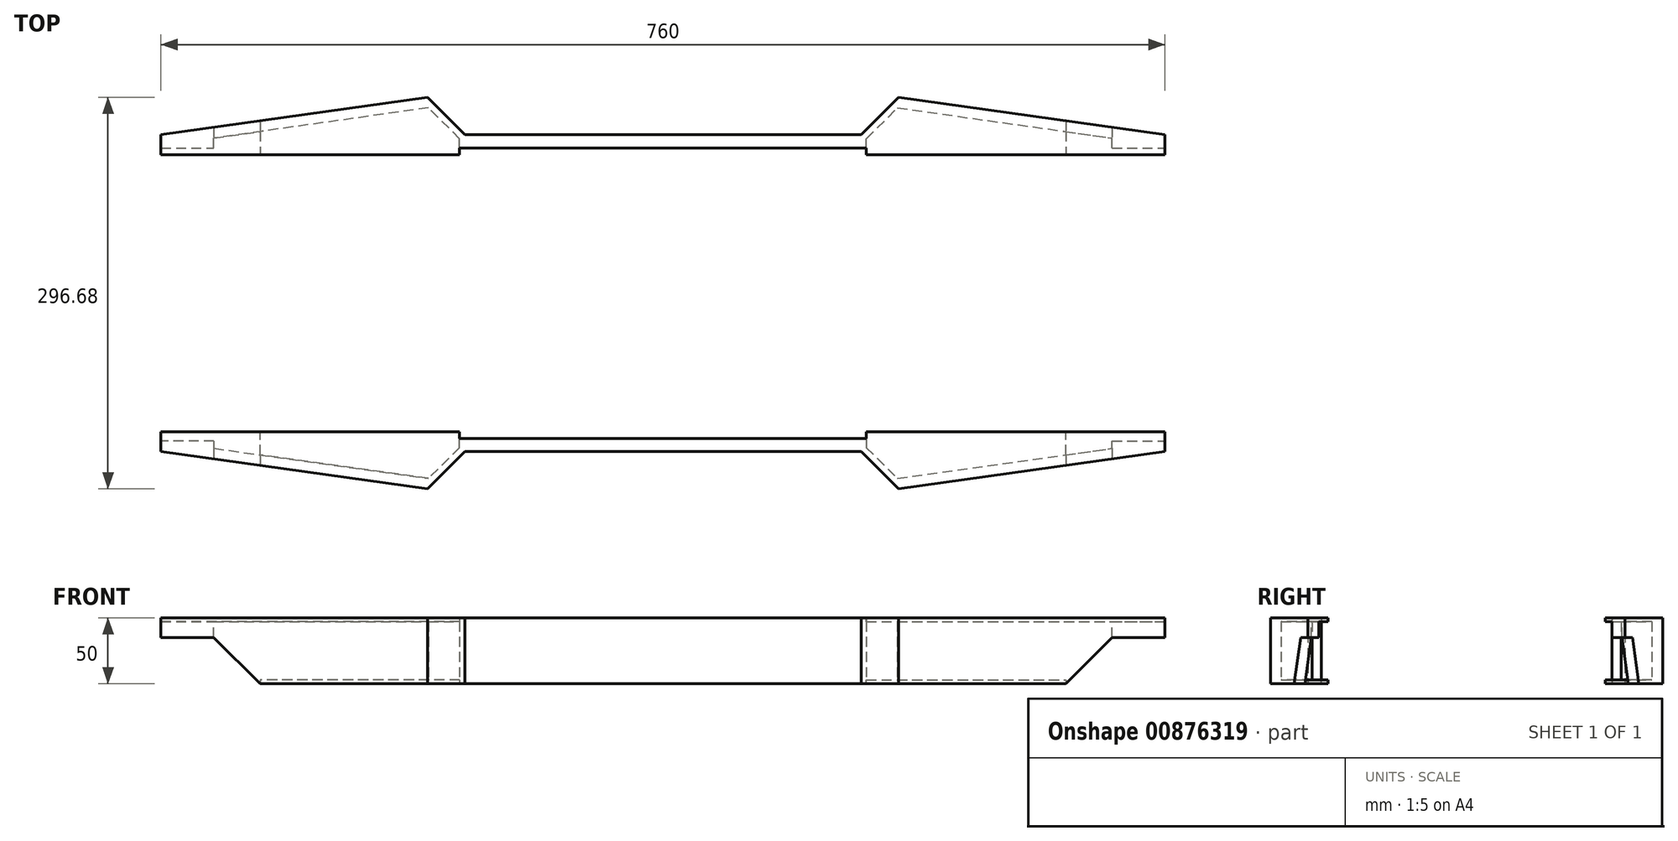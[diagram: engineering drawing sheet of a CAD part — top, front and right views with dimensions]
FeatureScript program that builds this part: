
annotation { "Feature Type Name" : "Feature", "Feature Type Description" : "" }
export const myFeature = defineFeature(function(context is Context, id is Id, definition is map)
    precondition{}
    {
        {
            var Q0;
            Q0=qCreatedBy(makeId("Top.planeOp"),FACE);
            var sketch = newSketch(context, id + "F0", { "sketchPlane" : qUnion([Q0])});
            skLineSegment(sketch, "E0", {"start": v(-380, 120) * mm, "end": v(-380, -120) * mm});
            skLineSegment(sketch, "E1", {"start": v(380, 120) * mm, "end": v(380, -120) * mm});
            skLineSegment(sketch, "E2", {"start": v(150, -120) * mm, "end": v(-150, -120) * mm});
            skLineSegment(sketch, "E3", {"start": v(-150, 120) * mm, "end": v(150, 120) * mm});
            skLineSegment(sketch, "E4", {"start": v(-160, 110) * mm, "end": v(160, 110) * mm, "construction": true});
            skLineSegment(sketch, "E5", {"start": v(160, 110) * mm, "end": v(160, -110) * mm, "construction": true});
            skLineSegment(sketch, "E6", {"start": v(160, -110) * mm, "end": v(-160, -110) * mm, "construction": true});
            skLineSegment(sketch, "E7", {"start": v(-160, -110) * mm, "end": v(-160, 110) * mm, "construction": true});
            skLineSegment(sketch, "E8.0", {"start": v(-150, -110) * mm, "end": v(-150, 110) * mm, "construction": true});
            skLineSegment(sketch, "E9.0", {"start": v(150, 110) * mm, "end": v(150, -110) * mm, "construction": true});
            skLineSegment(sketch, "E10", {"start": v(-150, -110) * mm, "end": v(-150, -120) * mm, "construction": true});
            skLineSegment(sketch, "E11", {"start": v(-150, 110) * mm, "end": v(-150, 120) * mm, "construction": true});
            skLineSegment(sketch, "E12", {"start": v(-150, 120) * mm, "end": v(-178.34, 148.34) * mm});
            skLineSegment(sketch, "E13", {"start": v(-380, 120) * mm, "end": v(-178.34, 148.34) * mm});
            skPoint(sketch, "E14.endSnap0", {"position": v(0, 110) * mm});
            skLineSegment(sketch, "E15.MirrorCS", {"start": v(150, 120) * mm, "end": v(178.34, 148.34) * mm});
            skLineSegment(sketch, "E16.MirrorCS", {"start": v(380, 120) * mm, "end": v(178.34, 148.34) * mm});
            skLineSegment(sketch, "E17.MirrorCS", {"start": v(-150, -120) * mm, "end": v(-178.34, -148.34) * mm, "construction": true});
            skLineSegment(sketch, "E18.MirrorCS", {"start": v(-380, -120) * mm, "end": v(-178.34, -148.34) * mm});
            skLineSegment(sketch, "E19.MirrorCS", {"start": v(150, -120) * mm, "end": v(178.34, -148.34) * mm});
            skLineSegment(sketch, "E20.MirrorCS", {"start": v(-150, -120) * mm, "end": v(-178.34, -148.34) * mm});
            skLineSegment(sketch, "E21.MirrorCS", {"start": v(380, -120) * mm, "end": v(178.34, -148.34) * mm});
            skSolve(sketch);
        }
        {
            var Q0;
            Q0=makeQuery(id+"F0.imprint","IMPRINT",FACE,{"disambiguationData":[TD([[makeQuery(id+"F0.imprint","IMPRINT",EDGE,{"derivedFrom":sQuery(id+"F0.wireOp",EDGE,"E0")}),1.0]])]});
            extrude(context, id + "F1", {"entities" : qUnion([Q0]), "depth" : 50 * mm, "offsetDistance" : 25 * mm});
        }
        {
            var Q0;
            Q0=makeQuery(id+"F1.opExtrude","SWEPT_FACE",FACE,{"disambiguationData":[OSD([sQuery(id+"F0.wireOp",EDGE,"E2")])]});
            var sketch = newSketch(context, id + "F2", { "sketchPlane" : qUnion([Q0])});
            skLineSegment(sketch, "E22", {"start": v(-380, 35) * mm, "end": v(-340, 35) * mm});
            skLineSegment(sketch, "E23", {"start": v(-340, 35) * mm, "end": v(-305, 0) * mm});
            skLineSegment(sketch, "E24", {"start": v(-380, 35) * mm, "end": v(-380, 0) * mm});
            skLineSegment(sketch, "E25", {"start": v(-380, 0) * mm, "end": v(-305, 0) * mm});
            skLineSegment(sketch, "E26.MirrorCS", {"start": v(380, 0) * mm, "end": v(305, 0) * mm});
            skLineSegment(sketch, "E27.MirrorCS", {"start": v(380, 35) * mm, "end": v(380, 0) * mm});
            skLineSegment(sketch, "E28.MirrorCS", {"start": v(380, 35) * mm, "end": v(340, 35) * mm});
            skLineSegment(sketch, "E29.MirrorCS", {"start": v(340, 35) * mm, "end": v(305, 0) * mm});
            skSolve(sketch);
        }
        {
            var Q0;
            Q0=makeQuery(id+"F1.opExtrude","SWEPT_FACE",FACE,{"disambiguationData":[OSD([sQuery(id+"F0.wireOp",EDGE,"E0")])]});
            var sketch = newSketch(context, id + "F3", { "sketchPlane" : qUnion([Q0])});
            skLineSegment(sketch, "E30.0", {"start": v(-110, 45) * mm, "end": v(110, 45) * mm});
            skLineSegment(sketch, "E31.0", {"start": v(-110, 5) * mm, "end": v(110, 5) * mm});
            skLineSegment(sketch, "E32.0", {"start": v(-110, 5) * mm, "end": v(-110, 45) * mm});
            skLineSegment(sketch, "E33.0", {"start": v(110, 45) * mm, "end": v(110, 5) * mm});
            skSolve(sketch);
        }
        {
            var Q0;
            Q0=makeQuery(id+"F3.imprint","IMPRINT",FACE,{"disambiguationData":[TD([[makeQuery(id+"F3.imprint","IMPRINT",EDGE,{"derivedFrom":sQuery(id+"F3.wireOp",EDGE,"E30.0")}),-1.0]])]});
            extrude(context, id + "F4", {"entities" : qUnion([Q0]), "operationType" : NewBodyOperationType.REMOVE, "oppositeDirection" : true, "depth" : 760 * mm, "offsetDistance" : 25 * mm});
        }
        {
            var Q0;
            Q0=makeQuery(id+"F2.imprint","IMPRINT",FACE,{"disambiguationData":[TD([[makeQuery(id+"F2.imprint","IMPRINT",EDGE,{"derivedFrom":sQuery(id+"F2.wireOp",EDGE,"E26.MirrorCS")}),-1.0]])]});
            var Q1;
            Q1=makeQuery(id+"F2.imprint","IMPRINT",FACE,{"disambiguationData":[TD([[makeQuery(id+"F2.imprint","IMPRINT",EDGE,{"derivedFrom":sQuery(id+"F2.wireOp",EDGE,"E22")}),-1.0]])]});
            extrude(context, id + "F5", {"entities" : qUnion([Q0, Q1]), "operationType" : NewBodyOperationType.REMOVE, "oppositeDirection" : true, "depth" : 240 * mm, "offsetDistance" : 25 * mm});
        }
        {
            var Q0;
            Q0=makeQuery(id+"F1.opExtrude","CAP_FACE",FACE,{"disambiguationData":[OSD([sQuery(id+"F0.wireOp",EDGE,"E0"),sQuery(id+"F0.wireOp",EDGE,"E1"),sQuery(id+"F0.wireOp",EDGE,"E2"),sQuery(id+"F0.wireOp",EDGE,"E3")])],"isStart":false});
            var sketch = newSketch(context, id + "F6", { "sketchPlane" : qUnion([Q0])});
            skLineSegment(sketch, "E34", {"start": v(-140, 90) * mm, "end": v(140, 90) * mm});
            skLineSegment(sketch, "E35", {"start": v(140, 90) * mm, "end": v(140, -90) * mm});
            skLineSegment(sketch, "E36", {"start": v(140, -90) * mm, "end": v(-140, -90) * mm});
            skLineSegment(sketch, "E37", {"start": v(-140, -90) * mm, "end": v(-140, 90) * mm});
            skLineSegment(sketch, "E38", {"start": v(160, 110) * mm, "end": v(160, -110) * mm});
            skLineSegment(sketch, "E39", {"start": v(-160, 110) * mm, "end": v(-160, -110) * mm});
            skLineSegment(sketch, "E40", {"start": v(-160, 110) * mm, "end": v(160, 110) * mm});
            skLineSegment(sketch, "E41", {"start": v(160, -110) * mm, "end": v(-160, -110) * mm});
            skSolve(sketch);
        }
        {
            var Q0;
            Q0=qSketchRegion(id+"F6",true);
            extrude(context, id + "F7", {"entities" : qUnion([Q0]), "operationType" : NewBodyOperationType.REMOVE, "oppositeDirection" : true, "depth" : 50 * mm, "offsetDistance" : 25 * mm});
        }
        {
            var Q0;
            Q0=qSketchRegion(id+"F2",true);
            extrude(context, id + "F8", {"entities" : qUnion([Q0]), "operationType" : NewBodyOperationType.REMOVE, "endBound" : BoundingType.SYMMETRIC, "oppositeDirection" : true, "depth" : 871.86 * mm, "offsetDistance" : 25 * mm});
        }
        {
            var Q0;
            {var subQ0=sQuery(id+"F0.wireOp",EDGE,"E18.MirrorCS");var subQ1=sQuery(id+"F0.wireOp",EDGE,"E16.MirrorCS");var subQ2=sQuery(id+"F0.wireOp",EDGE,"E15.MirrorCS");var subQ3=sQuery(id+"F0.wireOp",EDGE,"E13");var subQ4=sQuery(id+"F0.wireOp",EDGE,"E12");var subQ5=sQuery(id+"F0.wireOp",EDGE,"E19.MirrorCS");var subQ6=sQuery(id+"F0.wireOp",EDGE,"E0");var subQ7=sQuery(id+"F0.wireOp",EDGE,"E3");var subQ8=sQuery(id+"F0.wireOp",EDGE,"E1");var subQ9=sQuery(id+"F0.wireOp",EDGE,"E2");var subQ10=sQuery(id+"F0.wireOp",EDGE,"E20.MirrorCS");var subQ11=sQuery(id+"F0.wireOp",EDGE,"E21.MirrorCS");Q0=makeQuery(id+"F7.boolean.opBoolean","SPLIT",FACE,{"disambiguationData":[TD([makeQuery(id+"F1.opExtrude","SWEPT_FACE",FACE,{"disambiguationData":[OSD([subQ6])]})])],"derivedFrom":makeQuery(id+"F1.opExtrude","CAP_FACE",FACE,{"disambiguationData":[OSD([subQ6,subQ8,subQ9,subQ7,subQ4,subQ3,subQ2,subQ1,subQ0,subQ5,subQ10,subQ11])],"isStart":false})});}
            var sketch = newSketch(context, id + "F9", { "sketchPlane" : qUnion([Q0])});
            skLineSegment(sketch, "E42", {"start": v(-165, -110) * mm, "end": v(-305, -110) * mm});
            skLineSegment(sketch, "E43", {"start": v(-305, -110) * mm, "end": v(-305, 110) * mm});
            skLineSegment(sketch, "E44", {"start": v(-305, 110) * mm, "end": v(-165, 110) * mm});
            skLineSegment(sketch, "E45.0", {"start": v(-165, 110) * mm, "end": v(-165, -110) * mm});
            skLineSegment(sketch, "E46", {"start": v(0, 0) * mm, "end": v(0, 58.76) * mm});
            skLineSegment(sketch, "E47.MirrorCS", {"start": v(165, 110) * mm, "end": v(165, -110) * mm});
            skLineSegment(sketch, "E48.MirrorCS", {"start": v(165, -110) * mm, "end": v(305, -110) * mm});
            skLineSegment(sketch, "E49.MirrorCS", {"start": v(305, -110) * mm, "end": v(305, 110) * mm});
            skLineSegment(sketch, "E50.MirrorCS", {"start": v(305, 110) * mm, "end": v(165, 110) * mm});
            skSolve(sketch);
        }
        {
            var Q0;
            Q0=makeQuery(id+"F9.imprint","IMPRINT",FACE,{"disambiguationData":[TD([[makeQuery(id+"F9.imprint","IMPRINT",EDGE,{"derivedFrom":sQuery(id+"F9.wireOp",EDGE,"E42")}),-1.0]])]});
            var Q1;
            Q1=makeQuery(id+"F9.imprint","IMPRINT",FACE,{"disambiguationData":[TD([[makeQuery(id+"F9.imprint","IMPRINT",EDGE,{"derivedFrom":sQuery(id+"F9.wireOp",EDGE,"E47.MirrorCS")}),1.0]])]});
            extrude(context, id + "F10", {"entities" : qUnion([Q0, Q1]), "operationType" : NewBodyOperationType.REMOVE, "oppositeDirection" : true, "depth" : 10 * mm, "offsetDistance" : 25 * mm});
        }
        {
            var Q0;
            Q0=makeQuery(id+"F1.opExtrude","SWEPT_FACE",FACE,{"disambiguationData":[OSD([sQuery(id+"F0.wireOp",EDGE,"E2")])]});
            var sketch = newSketch(context, id + "F11", { "sketchPlane" : qUnion([Q0])});
            skLineSegment(sketch, "E51", {"start": v(-305, 50) * mm, "end": v(-305, 0) * mm});
            skLineSegment(sketch, "E52", {"start": v(-340, 50) * mm, "end": v(-340, 35) * mm});
            skLineSegment(sketch, "E53", {"start": v(-340, 35) * mm, "end": v(-305, 0) * mm});
            skLineSegment(sketch, "E54.0", {"start": v(-332.93, 35) * mm, "end": v(-305, 7.07) * mm});
            skLineSegment(sketch, "E55", {"start": v(-340, 35) * mm, "end": v(-332.93, 35) * mm});
            skLineSegment(sketch, "E56", {"start": v(0, 0) * mm, "end": v(0, 50) * mm});
            skLineSegment(sketch, "E57", {"start": v(-340, 35) * mm, "end": v(-346.55, 35) * mm});
            skLineSegment(sketch, "E58.MirrorCS", {"start": v(332.93, 35) * mm, "end": v(305, 7.07) * mm});
            skLineSegment(sketch, "E59.MirrorCS", {"start": v(340, 35) * mm, "end": v(305, 0) * mm});
            skLineSegment(sketch, "E60.MirrorCS", {"start": v(340, 35) * mm, "end": v(332.93, 35) * mm});
            skLineSegment(sketch, "E61", {"start": v(305, 7.07) * mm, "end": v(305, 0) * mm});
            skSolve(sketch);
        }
        {
            var Q0;
            {var subQ0=sQuery(id+"F11.wireOp",EDGE,"E53");Q0=makeQuery(id+"F11.imprint","IMPRINT",FACE,{"disambiguationData":[TD([[makeQuery(id+"F11.imprint","IMPRINT",EDGE,{"derivedFrom":subQ0}),1.0]])]});}
            var Q1;
            Q1=makeQuery(id+"F11.imprint","IMPRINT",FACE,{"disambiguationData":[TD([[makeQuery(id+"F11.imprint","IMPRINT",EDGE,{"derivedFrom":sQuery(id+"F11.wireOp",EDGE,"E58.MirrorCS")}),1.0]])]});
            extrude(context, id + "F12", {"entities" : qUnion([Q0, Q1]), "oppositeDirection" : true, "depth" : 240 * mm, "offsetDistance" : 25 * mm});
        }
        {
            var Q0;
            Q0=makeQuery(id+"F7.boolean.opBoolean","SPLIT",FACE,{"disambiguationData":[TD([makeQuery(id+"F7.opExtrude","SWEPT_FACE",FACE,{"disambiguationData":[OSD([sQuery(id+"F6.wireOp",EDGE,"E34")])]})])],"derivedFrom":makeQuery(id+"F1.opExtrude","CAP_FACE",FACE,{"disambiguationData":[OSD([sQuery(id+"F0.wireOp",EDGE,"E0"),sQuery(id+"F0.wireOp",EDGE,"E1"),sQuery(id+"F0.wireOp",EDGE,"E2"),sQuery(id+"F0.wireOp",EDGE,"E3"),sQuery(id+"F0.wireOp",EDGE,"E12"),sQuery(id+"F0.wireOp",EDGE,"E13"),sQuery(id+"F0.wireOp",EDGE,"E15.MirrorCS"),sQuery(id+"F0.wireOp",EDGE,"E16.MirrorCS"),sQuery(id+"F0.wireOp",EDGE,"E18.MirrorCS"),sQuery(id+"F0.wireOp",EDGE,"E19.MirrorCS"),sQuery(id+"F0.wireOp",EDGE,"E20.MirrorCS"),sQuery(id+"F0.wireOp",EDGE,"E21.MirrorCS")])],"isStart":false})});
            extrude(context, id + "F13", {"entities" : qUnion([Q0]), "operationType" : NewBodyOperationType.REMOVE, "oppositeDirection" : true, "depth" : 25 * mm, "offsetDistance" : 25 * mm});
        }
        {
            var Q0;
            Q0=makeQuery(id+"F7.boolean.opBoolean","SPLIT",FACE,{"disambiguationData":[TD([makeQuery(id+"F7.opExtrude","SWEPT_FACE",FACE,{"disambiguationData":[OSD([sQuery(id+"F6.wireOp",EDGE,"E34")])]})])],"derivedFrom":makeQuery(id+"F1.opExtrude","CAP_FACE",FACE,{"disambiguationData":[OSD([sQuery(id+"F0.wireOp",EDGE,"E0"),sQuery(id+"F0.wireOp",EDGE,"E1"),sQuery(id+"F0.wireOp",EDGE,"E2"),sQuery(id+"F0.wireOp",EDGE,"E3"),sQuery(id+"F0.wireOp",EDGE,"E12"),sQuery(id+"F0.wireOp",EDGE,"E13"),sQuery(id+"F0.wireOp",EDGE,"E15.MirrorCS"),sQuery(id+"F0.wireOp",EDGE,"E16.MirrorCS"),sQuery(id+"F0.wireOp",EDGE,"E18.MirrorCS"),sQuery(id+"F0.wireOp",EDGE,"E19.MirrorCS"),sQuery(id+"F0.wireOp",EDGE,"E20.MirrorCS"),sQuery(id+"F0.wireOp",EDGE,"E21.MirrorCS")])],"isStart":true})});
            extrude(context, id + "F14", {"entities" : qUnion([Q0]), "operationType" : NewBodyOperationType.REMOVE, "oppositeDirection" : true, "depth" : 25 * mm, "offsetDistance" : 25 * mm});
        }
        {
            var Q0;
            Q0=makeQuery(id+"F7.boolean.opBoolean","COPY",FACE,{"disambiguationData":[TD([makeQuery(id+"F4.boolean.opBoolean","COPY",FACE,{"derivedFrom":makeQuery(id+"F4.opExtrude","SWEPT_FACE",FACE,{"disambiguationData":[OSD([sQuery(id+"F3.wireOp",EDGE,"E30.0")])]})})])],"derivedFrom":makeQuery(id+"F7.opExtrude","SWEPT_FACE",FACE,{"disambiguationData":[OSD([sQuery(id+"F6.wireOp",EDGE,"E38")])]})});
            var sketch = newSketch(context, id + "F15", { "sketchPlane" : qUnion([Q0])});
            skLineSegment(sketch, "E62", {"start": v(-110, 45) * mm, "end": v(-110, 5) * mm});
            skLineSegment(sketch, "E63", {"start": v(-110, 45) * mm, "end": v(110, 45) * mm});
            skLineSegment(sketch, "E64", {"start": v(110, 45) * mm, "end": v(110, 5) * mm});
            skLineSegment(sketch, "E65", {"start": v(-110, 5) * mm, "end": v(110, 5) * mm});
            skSolve(sketch);
        }
        {
            var Q0;
            Q0=makeQuery(id+"F7.boolean.opBoolean","COPY",FACE,{"disambiguationData":[TD([makeQuery(id+"F4.boolean.opBoolean","COPY",FACE,{"derivedFrom":makeQuery(id+"F4.opExtrude","SWEPT_FACE",FACE,{"disambiguationData":[OSD([sQuery(id+"F3.wireOp",EDGE,"E31.0")])]})})])],"derivedFrom":makeQuery(id+"F7.opExtrude","SWEPT_FACE",FACE,{"disambiguationData":[OSD([sQuery(id+"F6.wireOp",EDGE,"E39")])]})});
            var sketch = newSketch(context, id + "F16", { "sketchPlane" : qUnion([Q0])});
            skLineSegment(sketch, "E66", {"start": v(-110, 5) * mm, "end": v(-110, 45) * mm});
            skLineSegment(sketch, "E67", {"start": v(-110, 5) * mm, "end": v(110, 5) * mm});
            skLineSegment(sketch, "E68", {"start": v(110, 5) * mm, "end": v(110, 45) * mm});
            skLineSegment(sketch, "E69", {"start": v(-110, 45) * mm, "end": v(110, 45) * mm});
            skSolve(sketch);
        }
        {
            var Q0;
            Q0=qSketchRegion(id+"F16",true);
            extrude(context, id + "F17", {"entities" : qUnion([Q0]), "operationType" : NewBodyOperationType.ADD, "oppositeDirection" : true, "depth" : 5 * mm, "offsetDistance" : 25 * mm});
        }
        {
            var Q0;
            Q0=makeQuery(id+"F15.imprint","IMPRINT",FACE,{"disambiguationData":[TD([[makeQuery(id+"F15.imprint","IMPRINT",EDGE,{"derivedFrom":sQuery(id+"F15.wireOp",EDGE,"E62")}),1.0]])]});
            extrude(context, id + "F18", {"entities" : qUnion([Q0]), "operationType" : NewBodyOperationType.ADD, "oppositeDirection" : true, "depth" : 5 * mm, "offsetDistance" : 25 * mm});
        }
        {
            var Q0;
            Q0=makeQuery(id+"F7.boolean.opBoolean","SPLIT",BODY,{"disambiguationData":[OD(0.0)],"derivedFrom":makeQuery(id+"F1.opExtrude","SWEPT_BODY",BODY,{"disambiguationData":[OSD([sQuery(id+"F0.wireOp",EDGE,"E0"),sQuery(id+"F0.wireOp",EDGE,"E1"),sQuery(id+"F0.wireOp",EDGE,"E2"),sQuery(id+"F0.wireOp",EDGE,"E3"),sQuery(id+"F0.wireOp",EDGE,"E12"),sQuery(id+"F0.wireOp",EDGE,"E13"),sQuery(id+"F0.wireOp",EDGE,"E15.MirrorCS"),sQuery(id+"F0.wireOp",EDGE,"E16.MirrorCS"),sQuery(id+"F0.wireOp",EDGE,"E18.MirrorCS"),sQuery(id+"F0.wireOp",EDGE,"E19.MirrorCS"),sQuery(id+"F0.wireOp",EDGE,"E20.MirrorCS"),sQuery(id+"F0.wireOp",EDGE,"E21.MirrorCS")])]})});
            var Q1;
            Q1=makeQuery(id+"F12.opExtrude","SWEPT_BODY",BODY,{"disambiguationData":[OSD([sQuery(id+"F11.wireOp",EDGE,"E51"),sQuery(id+"F11.wireOp",EDGE,"E53"),sQuery(id+"F11.wireOp",EDGE,"E54.0"),sQuery(id+"F11.wireOp",EDGE,"E55")])]});
            var Q2;
            Q2=makeQuery(id+"F12.opExtrude","SWEPT_BODY",BODY,{"disambiguationData":[OSD([sQuery(id+"F11.wireOp",EDGE,"E58.MirrorCS"),sQuery(id+"F11.wireOp",EDGE,"E59.MirrorCS"),sQuery(id+"F11.wireOp",EDGE,"E60.MirrorCS"),sQuery(id+"F11.wireOp",EDGE,"E61")])]});
            booleanBodies(context, id + "F19", {"operationType" : BooleanOperationType.UNION, "tools" : qUnion([Q0, Q1, Q2])});
        }
        {
            var Q0;
            Q0=makeQuery(id+"F10.boolean.opBoolean","COPY",FACE,{"derivedFrom":makeQuery(id+"F10.opExtrude","SWEPT_FACE",FACE,{"disambiguationData":[OSD([sQuery(id+"F9.wireOp",EDGE,"E43")])]})});
            extrude(context, id + "F20", {"entities" : qUnion([Q0]), "operationType" : NewBodyOperationType.REMOVE, "oppositeDirection" : true, "depth" : 121.6 * mm, "offsetDistance" : 25 * mm});
        }
        {
            var Q0;
            Q0=makeQuery(id+"F10.boolean.opBoolean","COPY",FACE,{"derivedFrom":makeQuery(id+"F10.opExtrude","SWEPT_FACE",FACE,{"disambiguationData":[OSD([sQuery(id+"F9.wireOp",EDGE,"E49.MirrorCS")])]})});
            extrude(context, id + "F21", {"entities" : qUnion([Q0]), "operationType" : NewBodyOperationType.REMOVE, "endBound" : BoundingType.SYMMETRIC, "depth" : 2865.48 * mm, "offsetDistance" : 25 * mm});
        }
        {
            var Q0;
            Q0=makeQuery(id+"F17.boolean.opBoolean","MERGE",FACE,{"derivedFrom":[makeQuery(id+"F10.boolean.opBoolean","COPY",FACE,{"derivedFrom":makeQuery(id+"F10.opExtrude","SWEPT_FACE",FACE,{"disambiguationData":[OSD([sQuery(id+"F9.wireOp",EDGE,"E45.0")])]})}),makeQuery(id+"F17.opExtrude","CAP_FACE",FACE,{"disambiguationData":[OSD([sQuery(id+"F16.wireOp",EDGE,"E66"),sQuery(id+"F16.wireOp",EDGE,"E67"),sQuery(id+"F16.wireOp",EDGE,"E68"),sQuery(id+"F16.wireOp",EDGE,"E69")])],"isStart":false})]});
            extrude(context, id + "F22", {"entities" : qUnion([Q0]), "operationType" : NewBodyOperationType.REMOVE, "endBound" : BoundingType.SYMMETRIC, "oppositeDirection" : true, "depth" : 1589.2 * mm, "offsetDistance" : 25 * mm});
        }
        {
            var Q0;
            {var subQ16=makeQuery(id+"F7.opExtrude","SWEPT_FACE",FACE,{"disambiguationData":[OSD([sQuery(id+"F6.wireOp",EDGE,"E39")])]});Q0=makeQuery(id+"F17.boolean.opBoolean","MERGE",FACE,{"derivedFrom":[makeQuery(id+"F7.boolean.opBoolean","COPY",FACE,{"disambiguationData":[TD([makeQuery(id+"F4.boolean.opBoolean","COPY",FACE,{"derivedFrom":makeQuery(id+"F4.opExtrude","SWEPT_FACE",FACE,{"disambiguationData":[OSD([sQuery(id+"F3.wireOp",EDGE,"E30.0")])]})})])],"derivedFrom":subQ16}),makeQuery(id+"F7.boolean.opBoolean","COPY",FACE,{"disambiguationData":[TD([makeQuery(id+"F4.boolean.opBoolean","COPY",FACE,{"derivedFrom":makeQuery(id+"F4.opExtrude","SWEPT_FACE",FACE,{"disambiguationData":[OSD([sQuery(id+"F3.wireOp",EDGE,"E31.0")])]})})])],"derivedFrom":subQ16}),makeQuery(id+"F17.opExtrude","CAP_FACE",FACE,{"disambiguationData":[OSD([sQuery(id+"F16.wireOp",EDGE,"E66"),sQuery(id+"F16.wireOp",EDGE,"E67"),sQuery(id+"F16.wireOp",EDGE,"E68"),sQuery(id+"F16.wireOp",EDGE,"E69")])],"isStart":true})]});}
            extrude(context, id + "F23", {"entities" : qUnion([Q0]), "operationType" : NewBodyOperationType.REMOVE, "endBound" : BoundingType.SYMMETRIC, "depth" : 1696.6 * mm, "offsetDistance" : 25 * mm});
        }
        {
            var Q0;
            {var subQ1=sQuery(id+"F0.wireOp",EDGE,"E19.MirrorCS");var subQ3=sQuery(id+"F0.wireOp",EDGE,"E21.MirrorCS");var subQ7=sQuery(id+"F0.wireOp",EDGE,"E2");var subQ8=makeQuery(id+"F1.opExtrude","SWEPT_FACE",FACE,{"disambiguationData":[OSD([subQ7])]});var subQ9=sQuery(id+"F0.wireOp",EDGE,"E18.MirrorCS");var subQ13=sQuery(id+"F0.wireOp",EDGE,"E20.MirrorCS");var subQ17=sQuery(id+"F0.wireOp",EDGE,"E16.MirrorCS");var subQ18=sQuery(id+"F0.wireOp",EDGE,"E15.MirrorCS");var subQ22=sQuery(id+"F0.wireOp",EDGE,"E3");var subQ23=sQuery(id+"F0.wireOp",EDGE,"E12");var subQ27=sQuery(id+"F0.wireOp",EDGE,"E13");Q0=makeQuery(id+"F23.boolean.opBoolean","SPLIT",FACE,{"disambiguationData":[TD([subQ8])],"derivedFrom":makeQuery(id+"F7.boolean.opBoolean","SPLIT",FACE,{"disambiguationData":[TD([subQ8])],"derivedFrom":makeQuery(id+"F1.opExtrude","CAP_FACE",FACE,{"disambiguationData":[OSD([sQuery(id+"F0.wireOp",EDGE,"E0"),sQuery(id+"F0.wireOp",EDGE,"E1"),subQ7,subQ22,subQ23,subQ27,subQ18,subQ17,subQ9,subQ1,subQ13,subQ3])],"isStart":true})})});}
            var sketch = newSketch(context, id + "F24", { "sketchPlane" : qUnion([Q0])});
            skLineSegment(sketch, "E70", {"start": v(-301, 110) * mm, "end": v(-154, 110) * mm});
            skLineSegment(sketch, "E71.0", {"start": v(-177.46, 140.39) * mm, "end": v(-301, 123.02) * mm});
            skLineSegment(sketch, "E72.0", {"start": v(-301, 123.02) * mm, "end": v(-301, 110) * mm});
            skLineSegment(sketch, "E73.0", {"start": v(-154, 116.93) * mm, "end": v(-177.46, 140.39) * mm});
            skLineSegment(sketch, "E74.0", {"start": v(-154, 110) * mm, "end": v(-154, 116.93) * mm});
            skLineSegment(sketch, "E75.MirrorCS", {"start": v(-301, -110) * mm, "end": v(-154, -110) * mm});
            skLineSegment(sketch, "E76.MirrorCS", {"start": v(-177.46, -140.39) * mm, "end": v(-301, -123.02) * mm});
            skLineSegment(sketch, "E77.MirrorCS", {"start": v(-301, -123.02) * mm, "end": v(-301, -110) * mm});
            skLineSegment(sketch, "E78.MirrorCS", {"start": v(-154, -116.93) * mm, "end": v(-177.46, -140.39) * mm});
            skLineSegment(sketch, "E79.MirrorCS", {"start": v(-154, -110) * mm, "end": v(-154, -116.93) * mm});
            skLineSegment(sketch, "E80.MirrorCS", {"start": v(154, 116.93) * mm, "end": v(177.46, 140.39) * mm});
            skLineSegment(sketch, "E81.MirrorCS", {"start": v(301, 110) * mm, "end": v(154, 110) * mm});
            skLineSegment(sketch, "E82.MirrorCS", {"start": v(301, -110) * mm, "end": v(154, -110) * mm});
            skLineSegment(sketch, "E83.MirrorCS", {"start": v(154, 110) * mm, "end": v(154, 116.93) * mm});
            skLineSegment(sketch, "E84.MirrorCS", {"start": v(177.46, 140.39) * mm, "end": v(301, 123.02) * mm});
            skLineSegment(sketch, "E85.MirrorCS", {"start": v(301, 123.02) * mm, "end": v(301, 110) * mm});
            skLineSegment(sketch, "E86.MirrorCS", {"start": v(154, -110) * mm, "end": v(154, -116.93) * mm});
            skLineSegment(sketch, "E87.MirrorCS", {"start": v(154, -116.93) * mm, "end": v(177.46, -140.39) * mm});
            skLineSegment(sketch, "E88.MirrorCS", {"start": v(301, -123.02) * mm, "end": v(301, -110) * mm});
            skLineSegment(sketch, "E89.MirrorCS", {"start": v(177.46, -140.39) * mm, "end": v(301, -123.02) * mm});
            skSolve(sketch);
        }
        {
            var Q0;
            Q0=makeQuery(id+"F24.imprint","IMPRINT",FACE,{"disambiguationData":[TD([[makeQuery(id+"F24.imprint","IMPRINT",EDGE,{"derivedFrom":sQuery(id+"F24.wireOp",EDGE,"E75.MirrorCS")}),-1.0]])]});
            var Q1;
            Q1=makeQuery(id+"F24.imprint","IMPRINT",FACE,{"disambiguationData":[TD([[makeQuery(id+"F24.imprint","IMPRINT",EDGE,{"derivedFrom":sQuery(id+"F24.wireOp",EDGE,"E86.MirrorCS")}),1.0]])]});
            extrude(context, id + "F25", {"entities" : qUnion([Q0, Q1]), "operationType" : NewBodyOperationType.REMOVE, "oppositeDirection" : true, "depth" : 50 * mm, "offsetDistance" : 25 * mm});
        }
        {
            var Q0;
            Q0=makeQuery(id+"F24.imprint","IMPRINT",FACE,{"disambiguationData":[TD([[makeQuery(id+"F24.imprint","IMPRINT",EDGE,{"derivedFrom":sQuery(id+"F24.wireOp",EDGE,"E70")}),-1.0]])]});
            var Q1;
            Q1=makeQuery(id+"F24.imprint","IMPRINT",FACE,{"disambiguationData":[TD([[makeQuery(id+"F24.imprint","IMPRINT",EDGE,{"derivedFrom":sQuery(id+"F24.wireOp",EDGE,"E80.MirrorCS")}),-1.0]])]});
            extrude(context, id + "F26", {"entities" : qUnion([Q0, Q1]), "operationType" : NewBodyOperationType.REMOVE, "oppositeDirection" : true, "depth" : 50 * mm, "offsetDistance" : 25 * mm});
        }
        {
            var Q0;
            {var subQ0=sQuery(id+"F0.wireOp",EDGE,"E2");var subQ1=makeQuery(id+"F1.opExtrude","SWEPT_FACE",FACE,{"disambiguationData":[OSD([subQ0])]});var subQ2=sQuery(id+"F0.wireOp",EDGE,"E1");var subQ4=sQuery(id+"F0.wireOp",EDGE,"E18.MirrorCS");var subQ6=sQuery(id+"F0.wireOp",EDGE,"E0");var subQ7=makeQuery(id+"F1.opExtrude","SWEPT_FACE",FACE,{"disambiguationData":[OSD([subQ6])]});var subQ8=sQuery(id+"F0.wireOp",EDGE,"E19.MirrorCS");var subQ10=sQuery(id+"F0.wireOp",EDGE,"E20.MirrorCS");var subQ12=sQuery(id+"F0.wireOp",EDGE,"E21.MirrorCS");var subQ15=sQuery(id+"F0.wireOp",EDGE,"E16.MirrorCS");var subQ16=sQuery(id+"F0.wireOp",EDGE,"E15.MirrorCS");var subQ17=sQuery(id+"F0.wireOp",EDGE,"E13");var subQ18=sQuery(id+"F0.wireOp",EDGE,"E12");var subQ19=sQuery(id+"F0.wireOp",EDGE,"E3");Q0=makeQuery(id+"F21.boolean.opBoolean","SPLIT",FACE,{"disambiguationData":[TD([subQ1])],"derivedFrom":makeQuery(id+"F7.boolean.opBoolean","SPLIT",FACE,{"disambiguationData":[TD([subQ7])],"derivedFrom":makeQuery(id+"F1.opExtrude","CAP_FACE",FACE,{"disambiguationData":[OSD([subQ6,subQ2,subQ0,subQ19,subQ18,subQ17,subQ16,subQ15,subQ4,subQ8,subQ10,subQ12])],"isStart":false})})});}
            var sketch = newSketch(context, id + "F27", { "sketchPlane" : qUnion([Q0])});
            skLineSegment(sketch, "E90.0", {"start": v(301, -123.02) * mm, "end": v(340, -117.54) * mm});
            skLineSegment(sketch, "E91", {"start": v(340, -110) * mm, "end": v(340, -117.54) * mm});
            skLineSegment(sketch, "E92", {"start": v(301, -110) * mm, "end": v(340, -110) * mm});
            skLineSegment(sketch, "E93", {"start": v(301, -110) * mm, "end": v(301, -123.02) * mm});
            skLineSegment(sketch, "E94.MirrorCS", {"start": v(-301, -110) * mm, "end": v(-301, -123.02) * mm});
            skLineSegment(sketch, "E95.MirrorCS", {"start": v(-301, -110) * mm, "end": v(-340, -110) * mm});
            skLineSegment(sketch, "E96.MirrorCS", {"start": v(-340, -110) * mm, "end": v(-340, -117.54) * mm});
            skLineSegment(sketch, "E97.MirrorCS", {"start": v(-301, -123.02) * mm, "end": v(-340, -117.54) * mm});
            skLineSegment(sketch, "E98.MirrorCS", {"start": v(340, 110) * mm, "end": v(340, 117.54) * mm});
            skLineSegment(sketch, "E99.MirrorCS", {"start": v(301, 110) * mm, "end": v(340, 110) * mm});
            skLineSegment(sketch, "E100.MirrorCS", {"start": v(301, 123.02) * mm, "end": v(340, 117.54) * mm});
            skLineSegment(sketch, "E101.MirrorCS", {"start": v(301, 110) * mm, "end": v(301, 123.02) * mm});
            skLineSegment(sketch, "E102.MirrorCS", {"start": v(-301, 110) * mm, "end": v(-301, 123.02) * mm});
            skLineSegment(sketch, "E103.MirrorCS", {"start": v(-301, 110) * mm, "end": v(-340, 110) * mm});
            skLineSegment(sketch, "E104.MirrorCS", {"start": v(-301, 123.02) * mm, "end": v(-340, 117.54) * mm});
            skLineSegment(sketch, "E105.MirrorCS", {"start": v(-340, 110) * mm, "end": v(-340, 117.54) * mm});
            skSolve(sketch);
        }
        {
            var Q0;
            Q0=qSketchRegion(id+"F27",true);
            extrude(context, id + "F28", {"entities" : qUnion([Q0]), "operationType" : NewBodyOperationType.REMOVE, "oppositeDirection" : true, "depth" : 50 * mm, "offsetDistance" : 25 * mm});
        }
        {
            var Q0;
            Q0=makeQuery(id+"F26.boolean.opBoolean","COPY",FACE,{"derivedFrom":makeQuery(id+"F26.opExtrude","SWEPT_FACE",FACE,{"disambiguationData":[OSD([sQuery(id+"F24.wireOp",EDGE,"E83.MirrorCS")])]})});
            var sketch = newSketch(context, id + "F29", { "sketchPlane" : qUnion([Q0])});
            skLineSegment(sketch, "E106", {"start": v(-110, 47) * mm, "end": v(-110, 3) * mm});
            skLineSegment(sketch, "E107.0", {"start": v(-112, 47) * mm, "end": v(-112, 3) * mm});
            skLineSegment(sketch, "E108.MirrorCS", {"start": v(110, 47) * mm, "end": v(110, 3) * mm});
            skLineSegment(sketch, "E109.MirrorCS", {"start": v(112, 47) * mm, "end": v(112, 3) * mm});
            skLineSegment(sketch, "E110", {"start": v(-110, 3) * mm, "end": v(-112, 3) * mm});
            skLineSegment(sketch, "E111", {"start": v(-110, 47) * mm, "end": v(-112, 47) * mm});
            skLineSegment(sketch, "E112.MirrorCS", {"start": v(110, 3) * mm, "end": v(112, 3) * mm});
            skLineSegment(sketch, "E113.MirrorCS", {"start": v(110, 47) * mm, "end": v(112, 47) * mm});
            skSolve(sketch);
        }
        {
            var Q0;
            Q0=makeQuery(id+"F29.imprint","IMPRINT",FACE,{"disambiguationData":[TD([[makeQuery(id+"F29.imprint","IMPRINT",EDGE,{"derivedFrom":sQuery(id+"F29.wireOp",EDGE,"E106")}),-1.0]])]});
            var Q1;
            Q1=makeQuery(id+"F29.imprint","IMPRINT",FACE,{"disambiguationData":[TD([[makeQuery(id+"F29.imprint","IMPRINT",EDGE,{"derivedFrom":sQuery(id+"F29.wireOp",EDGE,"ca43fbb2-e32b-444a-a71d-7a7fd8a9ca550.MirrorCS")}),1.0]])]});
            extrude(context, id + "F30", {"entities" : qUnion([Q0, Q1]), "operationType" : NewBodyOperationType.REMOVE, "endBound" : BoundingType.SYMMETRIC, "oppositeDirection" : true, "depth" : 1554.04 * mm, "offsetDistance" : 25 * mm});
        }
        {
            var Q0;
            Q0=makeQuery(id+"F29.imprint","IMPRINT",FACE,{"disambiguationData":[TD([[makeQuery(id+"F29.imprint","IMPRINT",EDGE,{"derivedFrom":sQuery(id+"F29.wireOp",EDGE,"E106")}),-1.0]])]});
            var Q1;
            Q1=makeQuery(id+"F29.imprint","IMPRINT",FACE,{"disambiguationData":[TD([[makeQuery(id+"F29.imprint","IMPRINT",EDGE,{"derivedFrom":sQuery(id+"F29.wireOp",EDGE,"ca43fbb2-e32b-444a-a71d-7a7fd8a9ca550.MirrorCS")}),1.0]])]});
            extrude(context, id + "F31", {"entities" : qUnion([Q0, Q1]), "operationType" : NewBodyOperationType.ADD, "oppositeDirection" : true, "depth" : 308 * mm, "offsetDistance" : 25 * mm});
        }
        {
            var Q0;
            {var subQ0=sQuery(id+"F0.wireOp",EDGE,"E12");var subQ2=sQuery(id+"F0.wireOp",EDGE,"E1");var subQ4=sQuery(id+"F0.wireOp",EDGE,"E3");var subQ5=makeQuery(id+"F1.opExtrude","SWEPT_FACE",FACE,{"disambiguationData":[OSD([subQ4])]});var subQ6=sQuery(id+"F0.wireOp",EDGE,"E0");var subQ7=makeQuery(id+"F1.opExtrude","SWEPT_FACE",FACE,{"disambiguationData":[OSD([subQ6])]});var subQ8=sQuery(id+"F0.wireOp",EDGE,"E13");var subQ10=sQuery(id+"F0.wireOp",EDGE,"E15.MirrorCS");var subQ12=sQuery(id+"F0.wireOp",EDGE,"E16.MirrorCS");var subQ15=sQuery(id+"F0.wireOp",EDGE,"E18.MirrorCS");var subQ16=sQuery(id+"F0.wireOp",EDGE,"E19.MirrorCS");var subQ17=sQuery(id+"F0.wireOp",EDGE,"E2");var subQ18=sQuery(id+"F0.wireOp",EDGE,"E20.MirrorCS");var subQ19=sQuery(id+"F0.wireOp",EDGE,"E21.MirrorCS");Q0=makeQuery(id+"F21.boolean.opBoolean","SPLIT",FACE,{"disambiguationData":[TD([subQ5])],"derivedFrom":makeQuery(id+"F7.boolean.opBoolean","SPLIT",FACE,{"disambiguationData":[TD([subQ7])],"derivedFrom":makeQuery(id+"F1.opExtrude","CAP_FACE",FACE,{"disambiguationData":[OSD([subQ6,subQ2,subQ17,subQ4,subQ0,subQ8,subQ10,subQ12,subQ15,subQ16,subQ18,subQ19])],"isStart":false})})});}
            var sketch = newSketch(context, id + "F32", { "sketchPlane" : qUnion([Q0])});
            skLineSegment(sketch, "E114", {"start": v(380, 110) * mm, "end": v(340, 110) * mm});
            skLineSegment(sketch, "E115", {"start": v(250.64, 241.62) * mm, "end": v(250.64, 241.62) * mm});
            skLineSegment(sketch, "E116.trimOffspring", {"start": v(-340, 110) * mm, "end": v(-380, 110) * mm});
            skLineSegment(sketch, "E117", {"start": v(-340, 105) * mm, "end": v(-380, 105) * mm});
            skLineSegment(sketch, "E118", {"start": v(340, 105) * mm, "end": v(380, 105) * mm});
            skLineSegment(sketch, "E119", {"start": v(380, 110) * mm, "end": v(380, 105) * mm});
            skLineSegment(sketch, "E120", {"start": v(-380, 105) * mm, "end": v(-380, 110) * mm});
            skLineSegment(sketch, "E121.MirrorCS", {"start": v(-154, -110) * mm, "end": v(-154, -105) * mm});
            skLineSegment(sketch, "E122.MirrorCS", {"start": v(-380, -105) * mm, "end": v(-380, -110) * mm});
            skLineSegment(sketch, "E123.MirrorCS", {"start": v(-340, -105) * mm, "end": v(-380, -105) * mm});
            skLineSegment(sketch, "E124.MirrorCS", {"start": v(-340, -110) * mm, "end": v(-380, -110) * mm});
            skLineSegment(sketch, "E125.MirrorCS", {"start": v(-340, -110) * mm, "end": v(-340, -105) * mm});
            skLineSegment(sketch, "E126.MirrorCS", {"start": v(154, -105) * mm, "end": v(154, -110) * mm});
            skLineSegment(sketch, "E127.MirrorCS", {"start": v(340, -105) * mm, "end": v(340, -110) * mm});
            skLineSegment(sketch, "E128.MirrorCS", {"start": v(380, -110) * mm, "end": v(380, -105) * mm});
            skLineSegment(sketch, "E129.MirrorCS", {"start": v(340, -105) * mm, "end": v(380, -105) * mm});
            skLineSegment(sketch, "E130.MirrorCS", {"start": v(380, -110) * mm, "end": v(340, -110) * mm});
            skLineSegment(sketch, "E131", {"start": v(-340, 110) * mm, "end": v(-340, 117.54) * mm});
            skLineSegment(sketch, "E132", {"start": v(-340, 117.54) * mm, "end": v(-177.46, 140.39) * mm});
            skLineSegment(sketch, "E133", {"start": v(-177.46, 140.39) * mm, "end": v(-154, 116.93) * mm});
            skLineSegment(sketch, "E134", {"start": v(-154, 116.93) * mm, "end": v(-154, 110) * mm});
            skLineSegment(sketch, "E135", {"start": v(-154, 105) * mm, "end": v(-340, 105) * mm});
            skLineSegment(sketch, "E136", {"start": v(154, 110) * mm, "end": v(154, 116.93) * mm});
            skLineSegment(sketch, "E137", {"start": v(154, 116.93) * mm, "end": v(177.46, 140.39) * mm});
            skLineSegment(sketch, "E138", {"start": v(177.46, 140.39) * mm, "end": v(340, 117.54) * mm});
            skLineSegment(sketch, "E139", {"start": v(340, 117.54) * mm, "end": v(340, 110) * mm});
            skLineSegment(sketch, "E140", {"start": v(340, 105) * mm, "end": v(154, 105) * mm});
            skLineSegment(sketch, "E141.MirrorCS", {"start": v(-154, -105) * mm, "end": v(-340, -105) * mm});
            skLineSegment(sketch, "E142.MirrorCS", {"start": v(-340, -117.54) * mm, "end": v(-177.46, -140.39) * mm});
            skLineSegment(sketch, "E143.MirrorCS", {"start": v(-340, -110) * mm, "end": v(-340, -117.54) * mm});
            skLineSegment(sketch, "E144.MirrorCS", {"start": v(-177.46, -140.39) * mm, "end": v(-154, -116.93) * mm});
            skLineSegment(sketch, "E145.MirrorCS", {"start": v(-154, -116.93) * mm, "end": v(-154, -110) * mm});
            skLineSegment(sketch, "E146.MirrorCS", {"start": v(154, -116.93) * mm, "end": v(177.46, -140.39) * mm});
            skLineSegment(sketch, "E147.MirrorCS", {"start": v(177.46, -140.39) * mm, "end": v(340, -117.54) * mm});
            skLineSegment(sketch, "E148.MirrorCS", {"start": v(154, -110) * mm, "end": v(154, -116.93) * mm});
            skLineSegment(sketch, "E149.MirrorCS", {"start": v(340, -117.54) * mm, "end": v(340, -110) * mm});
            skLineSegment(sketch, "E150.MirrorCS", {"start": v(340, -105) * mm, "end": v(154, -105) * mm});
            skLineSegment(sketch, "E151", {"start": v(-154, 110) * mm, "end": v(-154, 105) * mm});
            skLineSegment(sketch, "E152.MirrorCS", {"start": v(154, -110) * mm, "end": v(154, -105) * mm});
            skLineSegment(sketch, "E153.MirrorCS", {"start": v(154, 110) * mm, "end": v(154, 105) * mm});
            skSolve(sketch);
        }
        {
            var Q0;
            Q0 = qSketchRegion(id + "F32", true);
            extrude(context, id + "F33", {"entities" : qUnion([Q0]), "operationType" : NewBodyOperationType.ADD, "oppositeDirection" : true, "depth" : 3 * mm, "offsetDistance" : 25 * mm});
        }
        {
            var Q0;
            {var subQ0=sQuery(id+"F0.wireOp",EDGE,"E16.MirrorCS");var subQ4=sQuery(id+"F0.wireOp",EDGE,"E3");var subQ5=makeQuery(id+"F1.opExtrude","SWEPT_FACE",FACE,{"disambiguationData":[OSD([subQ4])]});var subQ8=sQuery(id+"F0.wireOp",EDGE,"E15.MirrorCS");var subQ11=sQuery(id+"F0.wireOp",EDGE,"E12");var subQ13=sQuery(id+"F0.wireOp",EDGE,"E13");var subQ17=sQuery(id+"F0.wireOp",EDGE,"E21.MirrorCS");var subQ18=sQuery(id+"F0.wireOp",EDGE,"E20.MirrorCS");var subQ19=sQuery(id+"F0.wireOp",EDGE,"E19.MirrorCS");var subQ20=sQuery(id+"F0.wireOp",EDGE,"E18.MirrorCS");var subQ21=sQuery(id+"F0.wireOp",EDGE,"E2");Q0=makeQuery(id+"F23.boolean.opBoolean","SPLIT",FACE,{"disambiguationData":[TD([subQ5])],"derivedFrom":makeQuery(id+"F7.boolean.opBoolean","SPLIT",FACE,{"disambiguationData":[TD([makeQuery(id+"F1.opExtrude","SWEPT_FACE",FACE,{"disambiguationData":[OSD([subQ21])]})])],"derivedFrom":makeQuery(id+"F1.opExtrude","CAP_FACE",FACE,{"disambiguationData":[OSD([sQuery(id+"F0.wireOp",EDGE,"E0"),sQuery(id+"F0.wireOp",EDGE,"E1"),subQ21,subQ4,subQ11,subQ13,subQ8,subQ0,subQ20,subQ19,subQ18,subQ17])],"isStart":true})})});}
            var sketch = newSketch(context, id + "F34", { "sketchPlane" : qUnion([Q0])});
            skLineSegment(sketch, "E154", {"start": v(-154, -110) * mm, "end": v(-154, -116.93) * mm});
            skLineSegment(sketch, "E155", {"start": v(-154, -116.93) * mm, "end": v(-177.46, -140.39) * mm});
            skLineSegment(sketch, "E156", {"start": v(-177.46, -140.39) * mm, "end": v(-305, -122.46) * mm});
            skLineSegment(sketch, "E157", {"start": v(-305, -122.46) * mm, "end": v(-305, -110) * mm});
            skLineSegment(sketch, "E158.0", {"start": v(-154, -105) * mm, "end": v(-305, -105) * mm});
            skLineSegment(sketch, "E159", {"start": v(-305, -110) * mm, "end": v(-305, -105) * mm});
            skLineSegment(sketch, "E160", {"start": v(-154, -105) * mm, "end": v(-154, -110) * mm});
            skLineSegment(sketch, "E161.MirrorCS", {"start": v(-154, 105) * mm, "end": v(-305, 105) * mm});
            skLineSegment(sketch, "E162.MirrorCS", {"start": v(-154, 116.93) * mm, "end": v(-177.46, 140.39) * mm});
            skLineSegment(sketch, "E163.MirrorCS", {"start": v(-177.46, 140.39) * mm, "end": v(-305, 122.46) * mm});
            skLineSegment(sketch, "E164.MirrorCS", {"start": v(-154, 105) * mm, "end": v(-154, 110) * mm});
            skLineSegment(sketch, "E165.MirrorCS", {"start": v(-154, 110) * mm, "end": v(-154, 116.93) * mm});
            skLineSegment(sketch, "E166.MirrorCS", {"start": v(-305, 110) * mm, "end": v(-305, 105) * mm});
            skLineSegment(sketch, "E167.MirrorCS", {"start": v(-305, 122.46) * mm, "end": v(-305, 110) * mm});
            skLineSegment(sketch, "E168.MirrorCS", {"start": v(154, -105) * mm, "end": v(154, -110) * mm});
            skLineSegment(sketch, "E169.MirrorCS", {"start": v(154, -110) * mm, "end": v(154, -116.93) * mm});
            skLineSegment(sketch, "E170.MirrorCS", {"start": v(154, -116.93) * mm, "end": v(177.46, -140.39) * mm});
            skLineSegment(sketch, "E171.MirrorCS", {"start": v(154, -105) * mm, "end": v(305, -105) * mm});
            skLineSegment(sketch, "E172.MirrorCS", {"start": v(305, -122.46) * mm, "end": v(305, -110) * mm});
            skLineSegment(sketch, "E173.MirrorCS", {"start": v(177.46, -140.39) * mm, "end": v(305, -122.46) * mm});
            skLineSegment(sketch, "E174.MirrorCS", {"start": v(305, -110) * mm, "end": v(305, -105) * mm});
            skLineSegment(sketch, "E175.MirrorCS", {"start": v(154, 105) * mm, "end": v(305, 105) * mm});
            skLineSegment(sketch, "E176.MirrorCS", {"start": v(177.46, 140.39) * mm, "end": v(305, 122.46) * mm});
            skLineSegment(sketch, "E177.MirrorCS", {"start": v(305, 122.46) * mm, "end": v(305, 110) * mm});
            skLineSegment(sketch, "E178.MirrorCS", {"start": v(305, 110) * mm, "end": v(305, 105) * mm});
            skLineSegment(sketch, "E179.MirrorCS", {"start": v(154, 105) * mm, "end": v(154, 110) * mm});
            skLineSegment(sketch, "E180.MirrorCS", {"start": v(154, 116.93) * mm, "end": v(177.46, 140.39) * mm});
            skLineSegment(sketch, "E181.MirrorCS", {"start": v(154, 110) * mm, "end": v(154, 116.93) * mm});
            skSolve(sketch);
        }
        {
            var Q0;
            Q0 = qSketchRegion(id + "F34", true);
            extrude(context, id + "F35", {"entities" : qUnion([Q0]), "operationType" : NewBodyOperationType.ADD, "oppositeDirection" : true, "depth" : 3 * mm, "offsetDistance" : 25 * mm});
        }
    });
